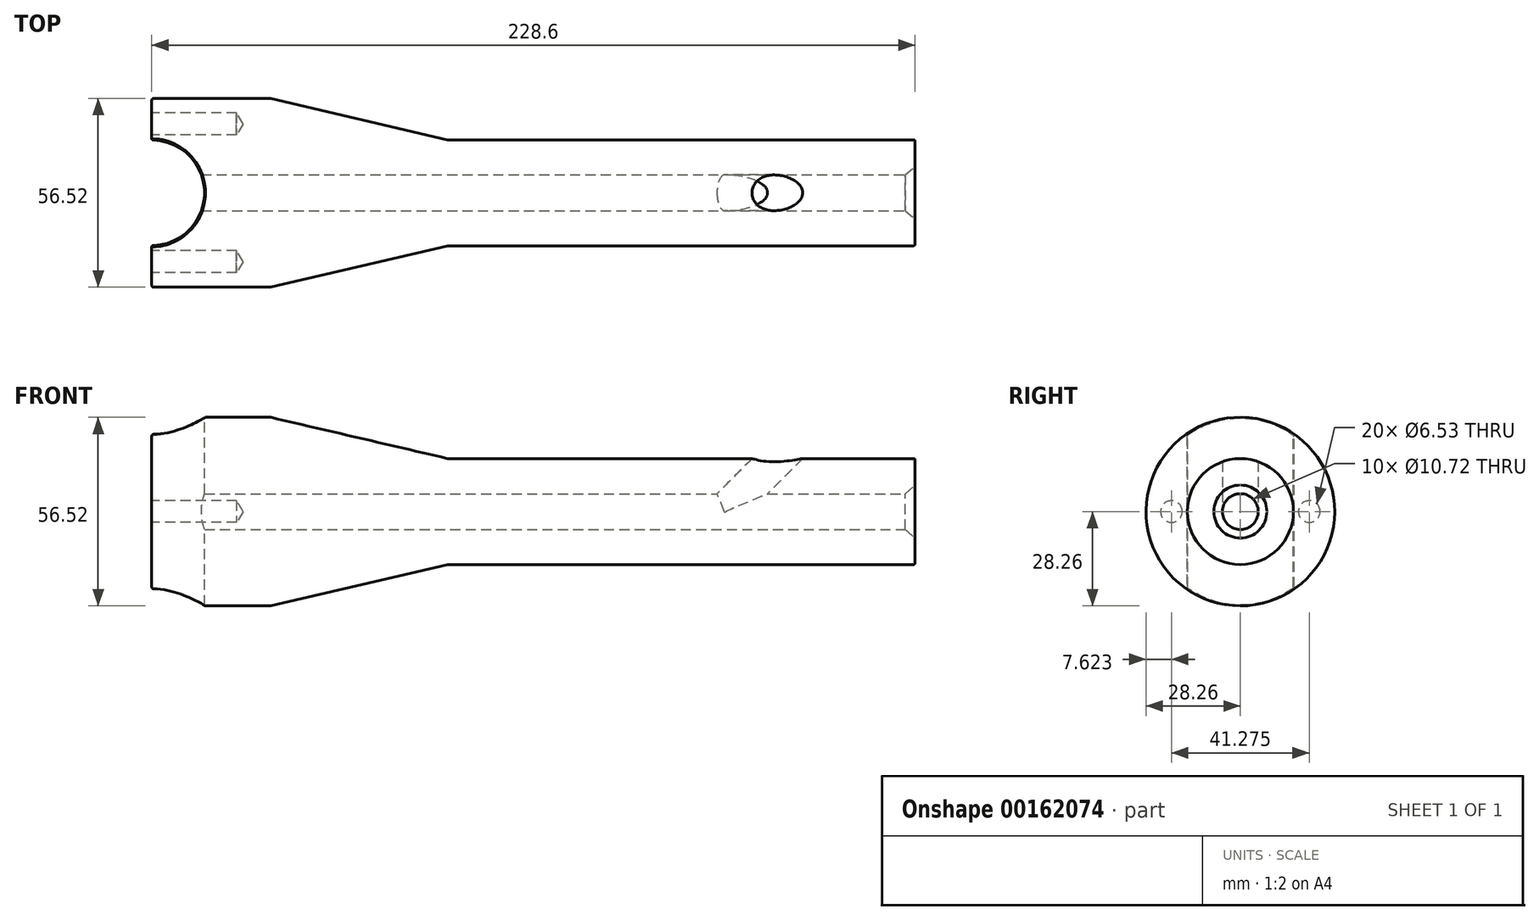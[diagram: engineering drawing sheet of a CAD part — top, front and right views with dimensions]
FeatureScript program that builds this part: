
annotation { "Feature Type Name" : "Feature", "Feature Type Description" : "" }
export const myFeature = defineFeature(function(context is Context, id is Id, definition is map)
    precondition{}
    {
        {
            var Q0;
            Q0=qCreatedBy(makeId("Front.planeOp"),FACE);
            var sketch = newSketch(context, id + "F0", { "sketchPlane" : qUnion([Q0])});
            skLineSegment(sketch, "E0", {"start": v(0, 0) * mm, "end": v(0, 28.26) * mm});
            skLineSegment(sketch, "E1", {"start": v(0, 28.26) * mm, "end": v(35.56, 28.26) * mm});
            skLineSegment(sketch, "E2", {"start": v(35.56, 28.26) * mm, "end": v(88.65, 15.87) * mm});
            skLineSegment(sketch, "E3", {"start": v(88.65, 15.87) * mm, "end": v(228.6, 15.87) * mm});
            skLineSegment(sketch, "E4", {"start": v(228.6, 15.87) * mm, "end": v(228.6, 0) * mm});
            skLineSegment(sketch, "E5", {"start": v(0, 0) * mm, "end": v(228.6, 0) * mm});
            skSolve(sketch);
        }
        {
            var Q0;
            Q0=qSketchRegion(id+"F0",true);
            var Q1;
            Q1=sQuery(id+"F0.wireOp",EDGE,"E5");
            revolve(context, id + "F1", {"entities" : qUnion([Q0]), "axis" : qUnion([Q1]), "revolveType" : RevolveType.FULL});
        }
        {
            var Q0;
            Q0=makeQuery(id+"F1.opRevolve","SWEPT_FACE",FACE,{"disambiguationData":[OSD([sQuery(id+"F0.wireOp",EDGE,"E4")])]});
            var sketch = newSketch(context, id + "F2", { "sketchPlane" : qUnion([Q0])});
            skPoint(sketch, "E6", {"position": v(0, 0) * mm});
            skSolve(sketch);
        }
        {
            var Q0;
            Q0=sQuery(id+"F2.wireOp",VERTEX,"E6");
            var Q1;
            Q1=makeQuery(id+"F1.opRevolve","SWEPT_BODY",BODY,{"disambiguationData":[OSD([sQuery(id+"F0.wireOp",EDGE,"E0"),sQuery(id+"F0.wireOp",EDGE,"E1"),sQuery(id+"F0.wireOp",EDGE,"E2"),sQuery(id+"F0.wireOp",EDGE,"E3"),sQuery(id+"F0.wireOp",EDGE,"E4"),sQuery(id+"F0.wireOp",EDGE,"E5")])]});
            hole(context, id + "F3", {"style" : HoleStyle.C_SINK, "endStyle" : HoleEndStyle.BLIND, "holeDiameter" : 10.72 * mm, "cSinkDiameter" : 15.88 * mm, "cSinkAngle" : 82 * degree, "holeDepth" : 38.1 * mm, "locations" : qUnion([Q0]), "scope" : qUnion([Q1])});
        }
        {
            var Q0;
            Q0=makeQuery(id+"F1.opRevolve","SWEPT_FACE",FACE,{"disambiguationData":[OSD([sQuery(id+"F0.wireOp",EDGE,"E0")])]});
            var sketch = newSketch(context, id + "F4", { "sketchPlane" : qUnion([Q0])});
            skPoint(sketch, "E7", {"position": v(0, 0) * mm});
            skSolve(sketch);
        }
        {
            var Q0;
            Q0=sQuery(id+"F4.wireOp",VERTEX,"E7");
            var Q1;
            Q1=makeQuery(id+"F1.opRevolve","SWEPT_BODY",BODY,{"disambiguationData":[OSD([sQuery(id+"F0.wireOp",EDGE,"E0"),sQuery(id+"F0.wireOp",EDGE,"E1"),sQuery(id+"F0.wireOp",EDGE,"E2"),sQuery(id+"F0.wireOp",EDGE,"E3"),sQuery(id+"F0.wireOp",EDGE,"E4"),sQuery(id+"F0.wireOp",EDGE,"E5")])]});
            hole(context, id + "F5", {"style" : HoleStyle.SIMPLE, "endStyle" : HoleEndStyle.BLIND, "holeDiameter" : 10.72 * mm, "holeDepth" : 191 * mm, "locations" : qUnion([Q0]), "scope" : qUnion([Q1])});
        }
        {
            var Q0;
            Q0=makeQuery(id+"F1.opRevolve","SWEPT_EDGE",EDGE,{"disambiguationData":[OSD([sQuery(id+"F0.wireOp",EDGE,"E0"),sQuery(id+"F0.wireOp",EDGE,"E1")])]});
            var Q1;
            Q1=makeQuery(id+"F1.opRevolve","SWEPT_EDGE",EDGE,{"disambiguationData":[OSD([sQuery(id+"F0.wireOp",EDGE,"E1"),sQuery(id+"F0.wireOp",EDGE,"E2")])]});
            var Q2;
            Q2=makeQuery(id+"F1.opRevolve","SWEPT_EDGE",EDGE,{"disambiguationData":[OSD([sQuery(id+"F0.wireOp",EDGE,"E2"),sQuery(id+"F0.wireOp",EDGE,"E3")])]});
            var Q3;
            Q3=makeQuery(id+"F1.opRevolve","SWEPT_EDGE",EDGE,{"disambiguationData":[OSD([sQuery(id+"F0.wireOp",EDGE,"E3"),sQuery(id+"F0.wireOp",EDGE,"E4")])]});
            fillet(context, id + "F6", {"entities" : qUnion([Q0, Q1, Q2, Q3]), "radius" : 0.5 * mm, "tangentPropagation" : true, "allowEdgeOverflow" : false});
        }
        {
            var Q0;
            Q0=qCreatedBy(makeId("Top.planeOp"),FACE);
            var sketch = newSketch(context, id + "F7", { "sketchPlane" : qUnion([Q0])});
            skPoint(sketch, "E8", {"position": v(0, 0) * mm});
            skCircle(sketch, "E9", {"center": v(0, 0) * mm, "radius": 15.81 * mm});
            skSolve(sketch);
        }
        {
            var Q0;
            Q0=makeQuery(id+"F7.imprint","IMPRINT",FACE,{"disambiguationData":[TD([[makeQuery(id+"F7.imprint","IMPRINT",EDGE,{"derivedFrom":sQuery(id+"F7.wireOp",EDGE,"E9")}),1.0]])]});
            extrude(context, id + "F8", {"entities" : qUnion([Q0]), "operationType" : NewBodyOperationType.REMOVE, "endBound" : BoundingType.THROUGH_ALL, "oppositeDirection" : true, "depth" : 25.4 * mm, "hasSecondDirection" : true, "secondDirectionBound" : SecondDirectionBoundingType.THROUGH_ALL, "secondDirectionOppositeDirection" : false, "secondDirectionDepth" : 25.4 * mm});
        }
        {
            var Q0;
            Q0=qCreatedBy(makeId("Top.planeOp"),FACE);
            var sketch = newSketch(context, id + "F9", { "sketchPlane" : qUnion([Q0])});
            skLineSegment(sketch, "E10", {"start": v(171.45, 61.21) * mm, "end": v(171.45, -62.5) * mm});
            skSolve(sketch);
        }
        {
            var Q0;
            Q0=sQuery(id+"F9.wireOp",EDGE,"E10");
            cPlane(context, id + "F10", {"entities" : qUnion([Q0]), "cplaneType" : CPlaneType.LINE_ANGLE, "offset" : 25.4 * mm, "angle" : 135 * degree, "width" : 152.4 * mm, "height" : 152.4 * mm});
        }
        {
            var Q0;
            Q0=qCreatedBy(id+"F10.planeOp",FACE);
            var sketch = newSketch(context, id + "F11", { "sketchPlane" : qUnion([Q0])});
            skCircle(sketch, "E11", {"center": v(0, -121.25) * mm, "radius": 5.36 * mm});
            skSolve(sketch);
        }
        {
            var Q0;
            Q0=qSketchRegion(id+"F11",true);
            extrude(context, id + "F12", {"entities" : qUnion([Q0]), "operationType" : NewBodyOperationType.REMOVE, "depth" : 32.77 * mm});
        }
        {
            var Q0;
            Q0=makeQuery(id+"F8.boolean.opBoolean","SPLIT",FACE,{"disambiguationData":[OD(1.0)],"derivedFrom":makeQuery(id+"F1.opRevolve","SWEPT_FACE",FACE,{"disambiguationData":[OSD([sQuery(id+"F0.wireOp",EDGE,"E0")])]})});
            var sketch = newSketch(context, id + "F13", { "sketchPlane" : qUnion([Q0])});
            skLineSegment(sketch, "E12", {"start": v(-27.75, 0) * mm, "end": v(27.72, 0) * mm});
            skPoint(sketch, "E13", {"position": v(-20.64, 0) * mm});
            skPoint(sketch, "E14", {"position": v(20.64, 0) * mm});
            skSolve(sketch);
        }
        {
            var Q0;
            Q0=sQuery(id+"F13.wireOp",VERTEX,"E13");
            var Q1;
            Q1=sQuery(id+"F13.wireOp",VERTEX,"E14");
            var Q2;
            Q2=makeQuery(id+"F1.opRevolve","SWEPT_BODY",BODY,{"disambiguationData":[OSD([sQuery(id+"F0.wireOp",EDGE,"E0"),sQuery(id+"F0.wireOp",EDGE,"E1"),sQuery(id+"F0.wireOp",EDGE,"E2"),sQuery(id+"F0.wireOp",EDGE,"E3"),sQuery(id+"F0.wireOp",EDGE,"E4"),sQuery(id+"F0.wireOp",EDGE,"E5")])]});
            hole(context, id + "F14", {"style" : HoleStyle.SIMPLE, "endStyle" : HoleEndStyle.BLIND, "standardTappedOrClearance" : lookupTablePath({ "standard" : "ANSI", "engagement" : "75%", "pitch" : "18 tpi", "size" : "5/16", "type" : "Tapped" }), "standardBlindInLast" : lookupTablePath({ "standard" : "ANSI", "engagement" : "75%", "pitch" : "18 tpi", "size" : "5/16", "type" : "Tapped" }), "holeDiameter" : 6.53 * mm, "holeDepth" : 25.4 * mm, "locations" : qUnion([Q0, Q1]), "scope" : qUnion([Q2]), "majorDiameter" : 7.94 * mm});
        }
        {
            var Q0;
            Q0=makeQuery(id+"F8.boolean.opBoolean","INTERSECT",EDGE,{"disambiguationData":[OD(1.0)],"derivedFrom":[makeQuery(id+"F1.opRevolve","SWEPT_FACE",FACE,{"disambiguationData":[OSD([sQuery(id+"F0.wireOp",EDGE,"E1")])]}),makeQuery(id+"F8.opExtrude","SWEPT_FACE",FACE,{"disambiguationData":[OSD([sQuery(id+"F7.wireOp",EDGE,"E9")])]})]});
            var Q1;
            Q1=makeQuery(id+"F8.boolean.opBoolean","INTERSECT",EDGE,{"disambiguationData":[OD(0.0)],"derivedFrom":[makeQuery(id+"F1.opRevolve","SWEPT_FACE",FACE,{"disambiguationData":[OSD([sQuery(id+"F0.wireOp",EDGE,"E1")])]}),makeQuery(id+"F8.opExtrude","SWEPT_FACE",FACE,{"disambiguationData":[OSD([sQuery(id+"F7.wireOp",EDGE,"E9")])]})]});
            chamfer(context, id + "F15", {"entities" : qUnion([Q0, Q1]), "width" : 0.25 * mm, "tangentPropagation" : true});
        }
    });
